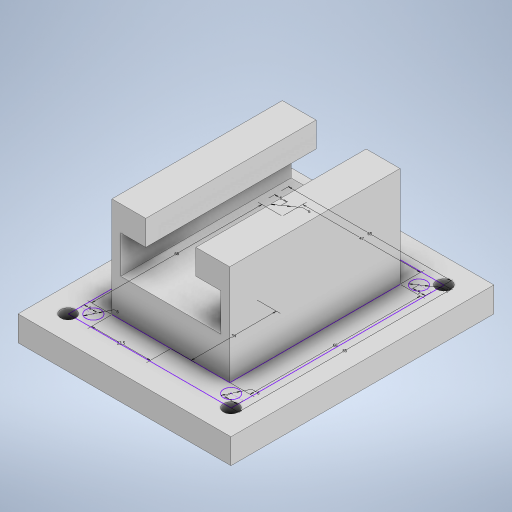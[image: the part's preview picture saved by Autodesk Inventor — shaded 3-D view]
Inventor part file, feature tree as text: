
AUTODESK INVENTOR PART (.ipt)
format: ipt  version: 2023 (Build 270158000, 158)  size: 313,344 bytes
history: native  units: mm
features: extrude x6, sketch x5
ambient origin geometry x8: Origin, YZ Plane, XZ Plane, XY Plane, X Axis, Y Axis, Z Axis, Center Point
bodies: Solid1 (feature_tree)
feature tree (11):
  sketch  "Sketch1"  dims[d0=65.0mm d1=85.0mm]
  sketch  "Sketch2"  dims[d2=34.0mm d3=23.5mm]
  extrude  "Extrusion1"  Depth=85.0mm
  extrude  "Extrusion2"  Depth=23.5mm
  extrude  "Extrusion3"  Depth=47.0mm
  extrude  "Extrusion4"  Depth=68.0mm
  sketch  "Sketch4"  dims[d6=68.0mm d8=5.0mm]
  sketch  "Sketch5"  dims[d9=6.0mm d11=5.0mm d12=6.0mm d14=5.0mm d15=6.0mm d17=5.0mm d18=6.0mm d19=10.0mm d20=0.0mm d21=20.0mm d22=0.0mm d23=40.0mm d24=0.0mm d25=13.5mm d26=13.5mm d27=10.0mm d28=10.0mm d29=15.0mm d30=40.0mm d31=15.0mm d32=10.0mm d33=68.0mm d34=0.0mm d37=85.0mm d38=105.0mm d41=6.0mm d42=105.0mm d43=6.0mm d44=6.0mm d45=6.0mm d46=10.0mm d47=0.0mm d48=10.0mm d49=0.0mm d50=0.5mm d51=0.872665mm]
  extrude  "Extrusion5"  Depth=10.0mm
  extrude  "Extrusion6"  Depth=10.0mm
  sketch  "Sketch3"  dims[d4=68.0mm d5=47.0mm]
